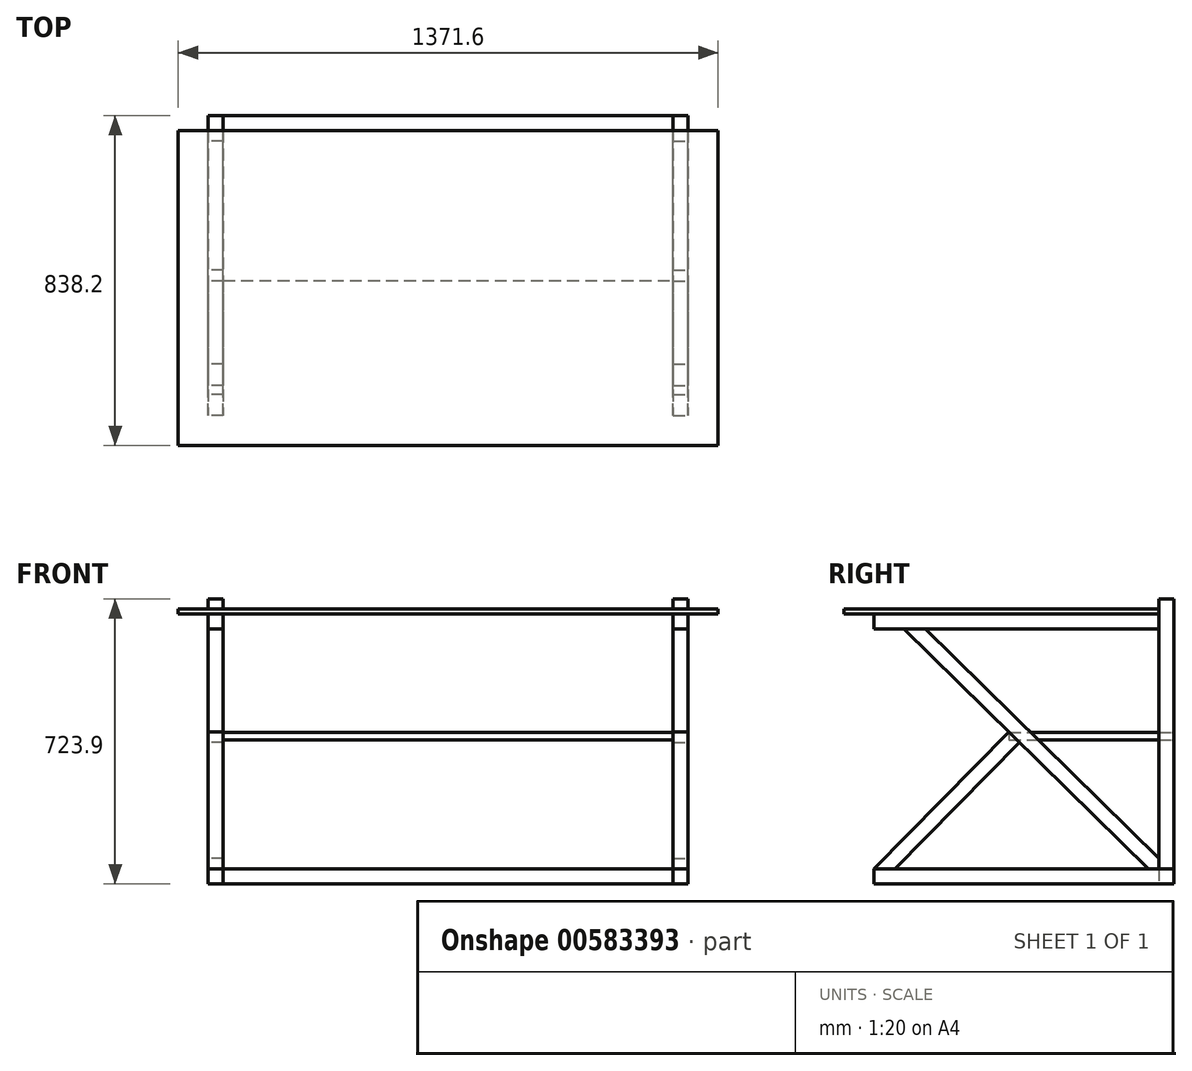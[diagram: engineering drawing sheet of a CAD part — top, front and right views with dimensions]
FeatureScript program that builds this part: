
annotation { "Feature Type Name" : "Feature", "Feature Type Description" : "" }
export const myFeature = defineFeature(function(context is Context, id is Id, definition is map)
    precondition{}
    {
        {
            var Q0;
            Q0=qCreatedBy(makeId("Top.planeOp"),FACE);
            var sketch = newSketch(context, id + "F0", { "sketchPlane" : qUnion([Q0])});
            skLineSegment(sketch, "E0.bottom", {"start": v(-571.5, -381) * mm, "end": v(-609.6, -381) * mm});
            skLineSegment(sketch, "E0.top", {"start": v(-571.5, 381) * mm, "end": v(-609.6, 381) * mm});
            skLineSegment(sketch, "E0.left", {"start": v(-571.5, -381) * mm, "end": v(-571.5, 381) * mm});
            skLineSegment(sketch, "E0.right", {"start": v(-609.6, -381) * mm, "end": v(-609.6, 381) * mm});
            skPoint(sketch, "E0.middle", {"position": v(-590.55, 0) * mm});
            skLineSegment(sketch, "E1.bottom", {"start": v(609.6, -381) * mm, "end": v(571.5, -381) * mm});
            skLineSegment(sketch, "E1.top", {"start": v(609.6, 381) * mm, "end": v(571.5, 381) * mm});
            skLineSegment(sketch, "E1.left", {"start": v(609.6, -381) * mm, "end": v(609.6, 381) * mm});
            skLineSegment(sketch, "E1.right", {"start": v(571.5, -381) * mm, "end": v(571.5, 381) * mm});
            skPoint(sketch, "E1.middle", {"position": v(590.55, 0) * mm});
            skSolve(sketch);
        }
        {
            var Q0;
            Q0 = qSketchRegion(id + "F0", true);
            extrude(context, id + "F1", {"entities" : qUnion([Q0]), "depth" : 38.1 * mm, "offsetDistance" : 25.4 * mm});
        }
        {
            var Q0;
            Q0=makeQuery(id+"F1.opExtrude","CAP_FACE",FACE,{"disambiguationData":[OSD([sQuery(id+"F0.wireOp",EDGE,"E0.bottom"),sQuery(id+"F0.wireOp",EDGE,"E0.top"),sQuery(id+"F0.wireOp",EDGE,"E0.left"),sQuery(id+"F0.wireOp",EDGE,"E0.right")])],"isStart":false});
            var sketch = newSketch(context, id + "F2", { "sketchPlane" : qUnion([Q0])});
            skLineSegment(sketch, "E2.bottom", {"start": v(-571.5, 381) * mm, "end": v(-609.6, 381) * mm});
            skLineSegment(sketch, "E2.top", {"start": v(-571.5, 342.9) * mm, "end": v(-609.6, 342.9) * mm});
            skLineSegment(sketch, "E2.left", {"start": v(-571.5, 381) * mm, "end": v(-571.5, 342.9) * mm});
            skLineSegment(sketch, "E2.right", {"start": v(-609.6, 381) * mm, "end": v(-609.6, 342.9) * mm});
            skLineSegment(sketch, "E3.bottom", {"start": v(571.5, 381) * mm, "end": v(609.6, 381) * mm});
            skLineSegment(sketch, "E3.top", {"start": v(571.5, 342.9) * mm, "end": v(609.6, 342.9) * mm});
            skLineSegment(sketch, "E3.left", {"start": v(571.5, 381) * mm, "end": v(571.5, 342.9) * mm});
            skLineSegment(sketch, "E3.right", {"start": v(609.6, 381) * mm, "end": v(609.6, 342.9) * mm});
            skSolve(sketch);
        }
        {
            var Q0;
            Q0 = qSketchRegion(id + "F2", true);
            extrude(context, id + "F3", {"entities" : qUnion([Q0]), "depth" : 685.8 * mm, "offsetDistance" : 25.4 * mm});
        }
        {
            var Q0;
            Q0=makeQuery(id+"F1.opExtrude","SWEPT_FACE",FACE,{"disambiguationData":[OSD([sQuery(id+"F0.wireOp",EDGE,"E1.left")])]});
            var sketch = newSketch(context, id + "F4", { "sketchPlane" : qUnion([Q0])});
            skLineSegment(sketch, "E4", {"start": v(342.9, 38.1) * mm, "end": v(342.9, 65.04) * mm});
            skLineSegment(sketch, "E5", {"start": v(342.9, 65.04) * mm, "end": v(-250.42, 647.7) * mm});
            skLineSegment(sketch, "E6", {"start": v(-250.42, 647.7) * mm, "end": v(-304.8, 647.7) * mm});
            skLineSegment(sketch, "E7", {"start": v(-304.8, 647.7) * mm, "end": v(315.96, 38.1) * mm});
            skLineSegment(sketch, "E8", {"start": v(315.96, 38.1) * mm, "end": v(342.9, 38.1) * mm});
            skSolve(sketch);
        }
        {
            var Q0;
            Q0 = qSketchRegion(id + "F4", true);
            extrude(context, id + "F5", {"entities" : qUnion([Q0]), "oppositeDirection" : true, "depth" : 38.1 * mm, "offsetDistance" : 25.4 * mm});
        }
        {
            var Q0;
            Q0=makeQuery(id+"F3.opExtrude","SWEPT_FACE",FACE,{"disambiguationData":[OSD([sQuery(id+"F2.wireOp",EDGE,"E3.top")])]});
            var sketch = newSketch(context, id + "F6", { "sketchPlane" : qUnion([Q0])});
            skLineSegment(sketch, "E9.bottom", {"start": v(-609.6, 647.7) * mm, "end": v(-571.5, 647.7) * mm});
            skLineSegment(sketch, "E9.top", {"start": v(-609.6, 685.8) * mm, "end": v(-571.5, 685.8) * mm});
            skLineSegment(sketch, "E9.left", {"start": v(-609.6, 647.7) * mm, "end": v(-609.6, 685.8) * mm});
            skLineSegment(sketch, "E9.right", {"start": v(-571.5, 647.7) * mm, "end": v(-571.5, 685.8) * mm});
            skPoint(sketch, "E9.middle", {"position": v(-590.55, 666.75) * mm});
            skLineSegment(sketch, "E10.bottom", {"start": v(571.5, 647.7) * mm, "end": v(609.6, 647.7) * mm});
            skLineSegment(sketch, "E10.top", {"start": v(571.5, 685.8) * mm, "end": v(609.6, 685.8) * mm});
            skLineSegment(sketch, "E10.left", {"start": v(571.5, 647.7) * mm, "end": v(571.5, 685.8) * mm});
            skLineSegment(sketch, "E10.right", {"start": v(609.6, 647.7) * mm, "end": v(609.6, 685.8) * mm});
            skPoint(sketch, "E10.middle", {"position": v(590.55, 666.75) * mm});
            skSolve(sketch);
        }
        {
            var Q0;
            Q0 = qSketchRegion(id + "F6", true);
            extrude(context, id + "F7", {"entities" : qUnion([Q0]), "depth" : 723.9 * mm, "offsetDistance" : 25.4 * mm});
        }
        {
            var Q0;
            Q0=makeQuery(id+"F5.opExtrude","SWEPT_BODY",BODY,{"disambiguationData":[OSD([sQuery(id+"F4.wireOp",EDGE,"E4"),sQuery(id+"F4.wireOp",EDGE,"E5"),sQuery(id+"F4.wireOp",EDGE,"E6"),sQuery(id+"F4.wireOp",EDGE,"E7"),sQuery(id+"F4.wireOp",EDGE,"E8")])]});
            var Q1;
            Q1=qCreatedBy(makeId("Right.planeOp"),FACE);
            mirror(context, id + "F8", {"entities" : qUnion([Q0]), "mirrorPlane" : qUnion([Q1])});
        }
        {
            var Q0;
            Q0=makeQuery(id+"F3.opExtrude","SWEPT_FACE",FACE,{"disambiguationData":[OSD([sQuery(id+"F2.wireOp",EDGE,"E3.left")])]});
            var sketch = newSketch(context, id + "F9", { "sketchPlane" : qUnion([Q0])});
            skLineSegment(sketch, "E11.bottom", {"start": v(38.1, 384.6) * mm, "end": v(-381, 384.6) * mm});
            skLineSegment(sketch, "E11.top", {"start": v(38.1, 365.55) * mm, "end": v(-381, 365.55) * mm});
            skLineSegment(sketch, "E11.left", {"start": v(38.1, 384.6) * mm, "end": v(38.1, 365.55) * mm});
            skLineSegment(sketch, "E11.right", {"start": v(-381, 384.6) * mm, "end": v(-381, 365.55) * mm});
            skLineSegment(sketch, "E12", {"start": v(-13.35, 388.67) * mm, "end": v(13.35, 361.49) * mm, "construction": true});
            skPoint(sketch, "E13", {"position": v(0, 375.08) * mm});
            skLineSegment(sketch, "E14", {"start": v(38.1, 375.08) * mm, "end": v(-381, 375.08) * mm, "construction": true});
            skSolve(sketch);
        }
        {
            var Q0;
            Q0 = qSketchRegion(id + "F9", true);
            var Q1;
            Q1=makeQuery(id+"F3.opExtrude","SWEPT_FACE",FACE,{"disambiguationData":[OSD([sQuery(id+"F2.wireOp",EDGE,"E2.left")])]});
            extrude(context, id + "F10", {"entities" : qUnion([Q0]), "endBound" : BoundingType.UP_TO_SURFACE, "depth" : 25.4 * mm, "endBoundEntityFace" : qUnion([Q1]), "offsetDistance" : 25.4 * mm});
        }
        {
            var Q0;
            Q0=makeQuery(id+"F7.opExtrude","SWEPT_FACE",FACE,{"disambiguationData":[OSD([sQuery(id+"F6.wireOp",EDGE,"E9.top")])]});
            var sketch = newSketch(context, id + "F11", { "sketchPlane" : qUnion([Q0])});
            skLineSegment(sketch, "E15.bottom", {"start": v(-685.8, 342.9) * mm, "end": v(685.8, 342.9) * mm});
            skLineSegment(sketch, "E15.top", {"start": v(-685.8, -457.2) * mm, "end": v(685.8, -457.2) * mm});
            skLineSegment(sketch, "E15.left", {"start": v(-685.8, 342.9) * mm, "end": v(-685.8, -457.2) * mm});
            skLineSegment(sketch, "E15.right", {"start": v(685.8, 342.9) * mm, "end": v(685.8, -457.2) * mm});
            skPoint(sketch, "E15.middle", {"position": v(0, -57.15) * mm});
            skSolve(sketch);
        }
        {
            var Q0;
            Q0 = qSketchRegion(id + "F11", true);
            extrude(context, id + "F12", {"entities" : qUnion([Q0]), "depth" : 12.7 * mm, "offsetDistance" : 25.4 * mm});
        }
        {
            var Q0;
            Q0=qCreatedBy(makeId("Right.planeOp"),FACE);
            var sketch = newSketch(context, id + "F13", { "sketchPlane" : qUnion([Q0])});
            skLineSegment(sketch, "E16.bottom", {"start": v(381, 0) * mm, "end": v(342.9, 0) * mm});
            skLineSegment(sketch, "E16.top", {"start": v(381, 38.1) * mm, "end": v(342.9, 38.1) * mm});
            skLineSegment(sketch, "E16.left", {"start": v(381, 0) * mm, "end": v(381, 38.1) * mm});
            skLineSegment(sketch, "E16.right", {"start": v(342.9, 0) * mm, "end": v(342.9, 38.1) * mm});
            skPoint(sketch, "E16.middle", {"position": v(361.95, 19.05) * mm});
            skSolve(sketch);
        }
        {
            var Q0;
            Q0 = qSketchRegion(id + "F13", true);
            extrude(context, id + "F14", {"entities" : qUnion([Q0]), "endBound" : BoundingType.UP_TO_NEXT, "depth" : 25.4 * mm, "offsetDistance" : 25.4 * mm, "hasSecondDirection" : true, "secondDirectionBound" : SecondDirectionBoundingType.UP_TO_NEXT, "secondDirectionOppositeDirection" : true, "secondDirectionDepth" : 25.4 * mm});
        }
        {
            var Q0;
            Q0=makeQuery(id+"F5.opExtrude","CAP_FACE",FACE,{"disambiguationData":[OSD([sQuery(id+"F4.wireOp",EDGE,"E4"),sQuery(id+"F4.wireOp",EDGE,"E5"),sQuery(id+"F4.wireOp",EDGE,"E6"),sQuery(id+"F4.wireOp",EDGE,"E7"),sQuery(id+"F4.wireOp",EDGE,"E8")])],"isStart":true});
            var sketch = newSketch(context, id + "F15", { "sketchPlane" : qUnion([Q0])});
            skLineSegment(sketch, "E17", {"start": v(-381, 38.1) * mm, "end": v(-327.6, 38.1) * mm});
            skLineSegment(sketch, "E18", {"start": v(-327.6, 38.1) * mm, "end": v(-11.66, 359.83) * mm});
            skLineSegment(sketch, "E19", {"start": v(-11.66, 359.83) * mm, "end": v(-38.84, 386.52) * mm});
            skLineSegment(sketch, "E20", {"start": v(-38.84, 386.52) * mm, "end": v(-381, 38.1) * mm});
            skSolve(sketch);
        }
        {
            var Q0;
            Q0 = qSketchRegion(id + "F15", true);
            extrude(context, id + "F16", {"entities" : qUnion([Q0]), "oppositeDirection" : true, "depth" : 38.1 * mm, "offsetDistance" : 25.4 * mm});
        }
        {
            var Q0;
            Q0=makeQuery(id+"F16.opExtrude","SWEPT_BODY",BODY,{"disambiguationData":[OSD([sQuery(id+"F15.wireOp",EDGE,"E17"),sQuery(id+"F15.wireOp",EDGE,"E18"),sQuery(id+"F15.wireOp",EDGE,"E19"),sQuery(id+"F15.wireOp",EDGE,"E20")])]});
            var Q1;
            Q1=qCreatedBy(makeId("Right.planeOp"),FACE);
            mirror(context, id + "F17", {"entities" : qUnion([Q0]), "mirrorPlane" : qUnion([Q1])});
        }
    });
